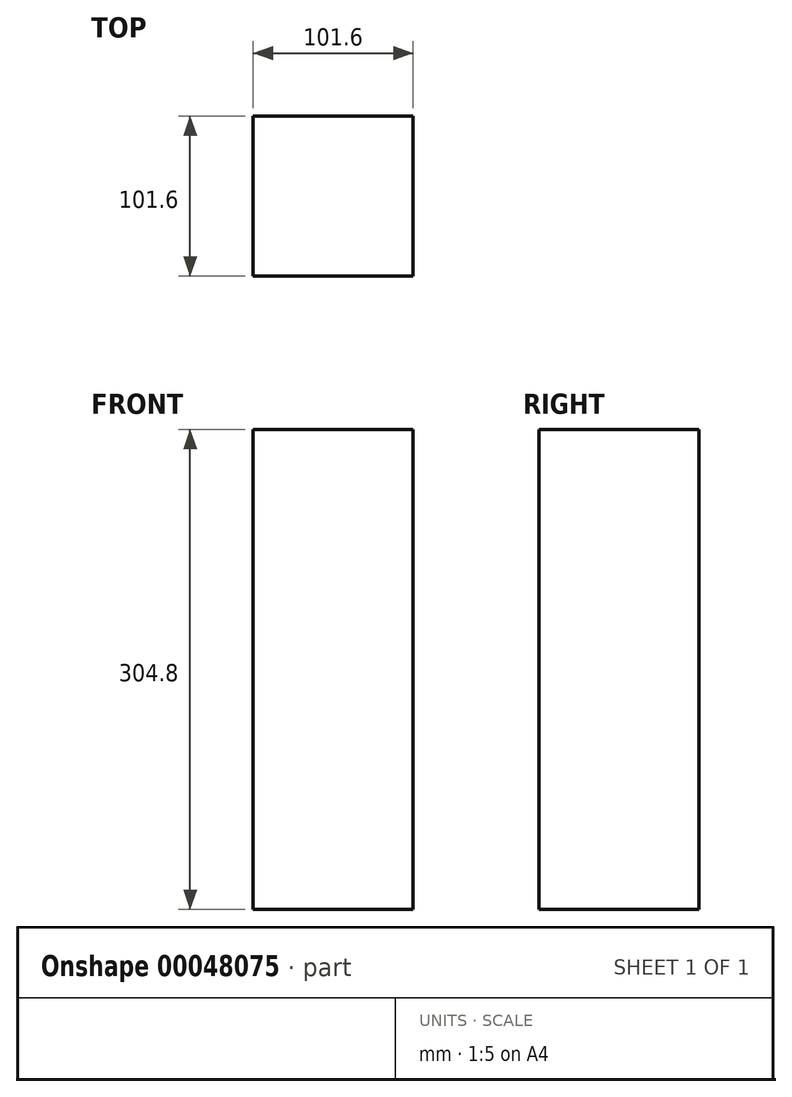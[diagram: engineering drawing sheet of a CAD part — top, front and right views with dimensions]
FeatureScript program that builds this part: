
annotation { "Feature Type Name" : "Feature", "Feature Type Description" : "" }
export const myFeature = defineFeature(function(context is Context, id is Id, definition is map)
    precondition{}
    {
        {
            var Q0;
            Q0=qCreatedBy(makeId("Top.planeOp"),FACE);
            var sketch = newSketch(context, id + "F0", { "sketchPlane" : qUnion([Q0])});
            skLineSegment(sketch, "E0.bottom", {"start": v(-50.8, 50.8) * mm, "end": v(50.8, 50.8) * mm});
            skLineSegment(sketch, "E0.top", {"start": v(-50.8, -50.8) * mm, "end": v(50.8, -50.8) * mm});
            skLineSegment(sketch, "E0.left", {"start": v(-50.8, 50.8) * mm, "end": v(-50.8, -50.8) * mm});
            skLineSegment(sketch, "E0.right", {"start": v(50.8, 50.8) * mm, "end": v(50.8, -50.8) * mm});
            skSolve(sketch);
        }
        {
            var Q0;
            Q0=makeQuery(id+"F0.imprint","IMPRINT",FACE,{"disambiguationData":[TD([[makeQuery(id+"F0.imprint","IMPRINT",EDGE,{"derivedFrom":sQuery(id+"F0.wireOp",EDGE,"E0.bottom")}),-1.0]])]});
            extrude(context, id + "F1", {"entities" : qUnion([Q0]), "endBound" : BoundingType.SYMMETRIC, "depth" : 304.8 * mm});
        }
    });
